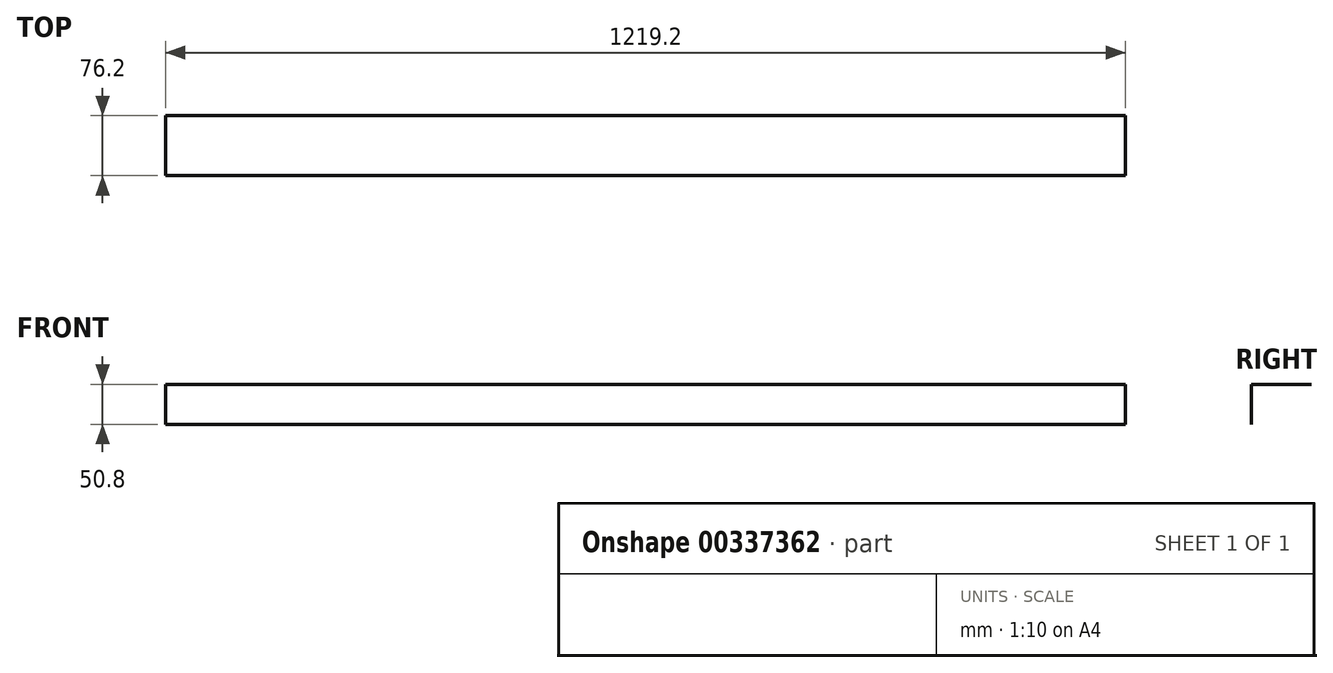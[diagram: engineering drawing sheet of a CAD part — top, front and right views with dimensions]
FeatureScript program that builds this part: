
annotation { "Feature Type Name" : "Feature", "Feature Type Description" : "" }
export const myFeature = defineFeature(function(context is Context, id is Id, definition is map)
    precondition{}
    {
        {
            var Q0;
            Q0=qCreatedBy(makeId("Right.planeOp"),FACE);
            var sketch = newSketch(context, id + "F0", { "sketchPlane" : qUnion([Q0])});
            skLineSegment(sketch, "E0", {"start": v(9.12, -62.56) * mm, "end": v(9.12, -11.76) * mm});
            skLineSegment(sketch, "E1", {"start": v(9.12, -11.76) * mm, "end": v(85.32, -11.76) * mm});
            skSolve(sketch);
        }
        {
            var Q0;
            Q0 = qSketchRegion(id + "F0", true);
            var Q1;
            Q1=sQuery(id+"F0.wireOp",EDGE,"E1");
            var Q2;
            Q2=sQuery(id+"F0.wireOp",EDGE,"E0");
            extrude(context, id + "F1", {"entities" : qUnion([Q0]), "bodyType" : ToolBodyType.SURFACE, "surfaceEntities" : qUnion([Q1, Q2]), "depth" : 1219.2 * mm});
        }
    });
